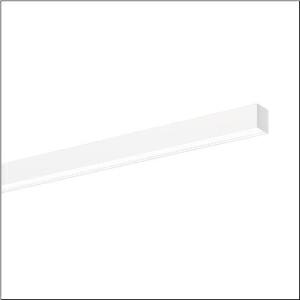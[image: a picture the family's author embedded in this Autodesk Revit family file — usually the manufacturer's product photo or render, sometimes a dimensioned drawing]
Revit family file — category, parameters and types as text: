
# Revit family: silica_r__21_51mx23db45wb_81de
name_source: partatom
category: Lighting Fixtures
units: mm (PartAtom-declared; Revit-internal decimal feet)

## family parameters
Cut with Voids When Loaded = No
Host = Face
Light Source = No
Part Type = Normal
Room Calculation Point = No
Round Connector Dimension = Use Diameter
Shared = No

## types (1)
- --- (1 x LED, 4100 lm, 28.1 W, 4000K)
    Apparent Load = 28 VA
    CIE Flux Codes = 78 96 99 100 100
    Color Rendering = 80
    Color Temperature = 4000K
    Default Elevation = 1800 mm
    Description = Silica® 21, office luminaire, primary optical cover: prismatic diffuser, of PMMA, CAT 2 (L<= 3000cd/m²), light emission: direct distribution, primary light characteristic: symmetric, installation type: surface-mounted, LED, rated luminous flux: 4.100lm, luminous efficacy: 146lm/W, light colour: 840, colour temperature: 4000K, with terminal, 3+2-pole, max. 2.5mm², mains connection: 220..240V, AC, 50/60Hz, rated input power: 28.1W, luminaire housing, of aluminium, traffic white (RAL 9016), length: 1.504mm, width: 53mm, height: 53mm, protection rating (complete): IP20, insulation class (complete): insulation class I (protective earthing), certification: CE, permissible operating ambient temperature: 0..+35°C, standard: EN 50419, packaging unit: 1 piece
    Height = 0 mm  [stored 0 ft]
    Lamp = 1 x LED
    Lamp Light Flux = 4100 lm
    Lamp Power = 28.1 W
    Lamp count = 1
    Length = 1504 mm
    Luminous efficacy = 146 lm/W
    Manufacturer = Siteco
    ModVariant = No
    Model = 51MX23DB45WB
    Mounting Place = Ceiling
    Mounting Type = Recessed
    Number of Poles = 1
    OnlyDefault = Yes
    Power Factor = 1
    Product Name = Silica® 21
    Product group = office luminaire | ceiling recessed
    ProductGroupID = 400
    Protection Class = Protection class I
    Protection Degree = IP 20
    RLX_Detail_Level = 1
    RLX_Emergency_Light_Flux = 0 lm
    RLX_Emergency_Type = 0
    RLX_Emergency_Type_DB = No
    RlxData = <blob elided: 18837 chars, md5=862f178b>
    Socket = socket
    Standby Power = 0 W
    System Light Flux = 4100 lm
    System Power = 28 W
    Type Comments = factory setting: luminous flux: 100 % | dim-lin: 254 | 323 mA
    Type Image = l_1335877.jpg
    URL = http://relux.com
    VarID = @adj_089009
    Voltage = 0 V
    Weight = 0.00 kg
    Width = 53 mm

note: [stored X ft] marks values corroborated as IEEE doubles in the binary element streams (Revit-internal decimal feet)

## geometry (parser evidence)
native form markers: Blend x4, Sweep x9
no freeform markers — native parametric forms only
